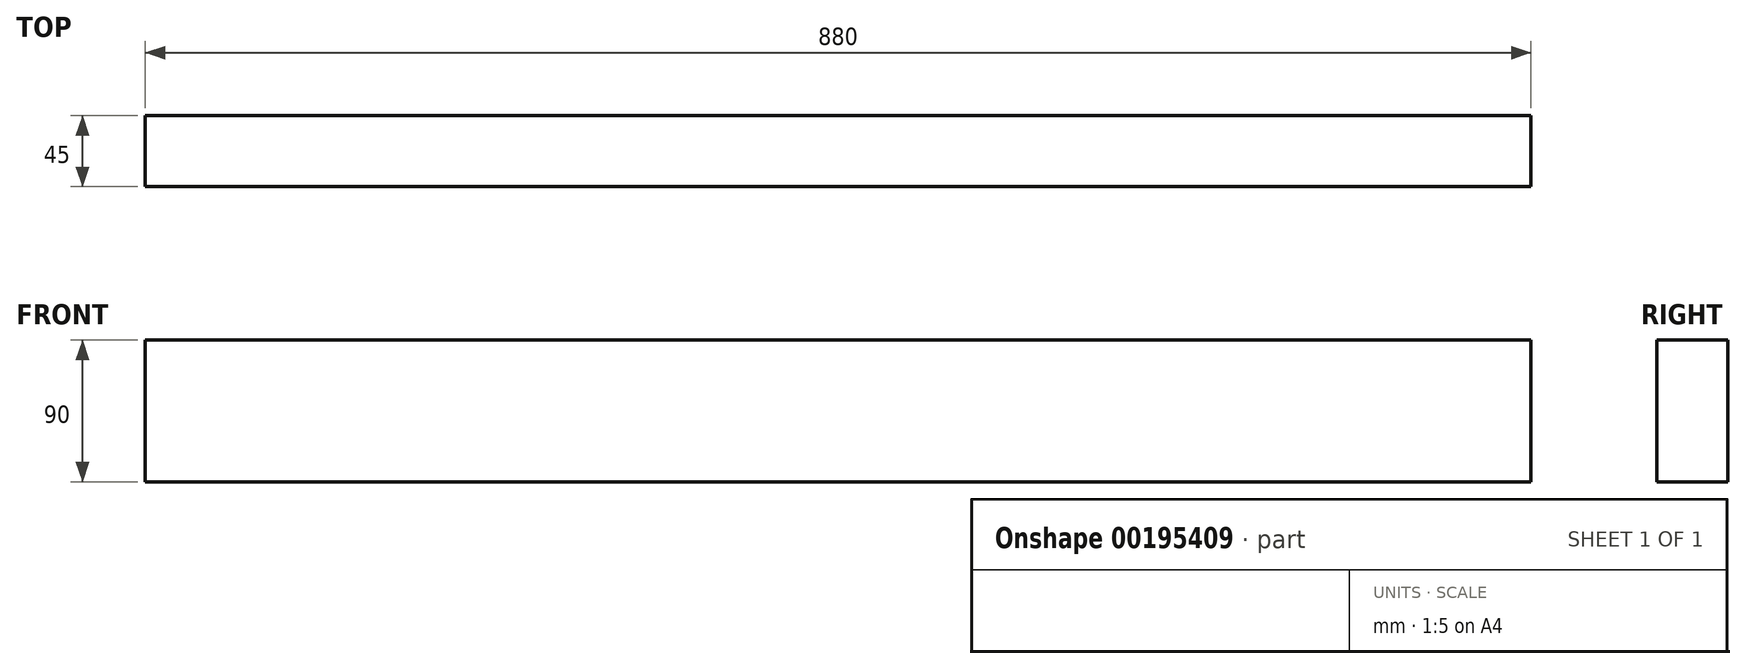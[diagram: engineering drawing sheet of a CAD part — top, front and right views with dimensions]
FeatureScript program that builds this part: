
annotation { "Feature Type Name" : "Feature", "Feature Type Description" : "" }
export const myFeature = defineFeature(function(context is Context, id is Id, definition is map)
    precondition{}
    {
        {
            var Q0;
            Q0=qCreatedBy(makeId("Front.planeOp"),FACE);
            var sketch = newSketch(context, id + "F0", { "sketchPlane" : qUnion([Q0])});
            skLineSegment(sketch, "E0.bottom", {"start": v(440, -45) * mm, "end": v(-440, -45) * mm});
            skLineSegment(sketch, "E0.top", {"start": v(440, 45) * mm, "end": v(-440, 45) * mm});
            skLineSegment(sketch, "E0.left", {"start": v(440, -45) * mm, "end": v(440, 45) * mm});
            skLineSegment(sketch, "E0.right", {"start": v(-440, -45) * mm, "end": v(-440, 45) * mm});
            skPoint(sketch, "E0.middle", {"position": v(0, 0) * mm});
            skSolve(sketch);
        }
        {
            var Q0;
            Q0=makeQuery(id+"F0.imprint","IMPRINT",FACE,{"disambiguationData":[TD([[makeQuery(id+"F0.imprint","IMPRINT",EDGE,{"derivedFrom":sQuery(id+"F0.wireOp",EDGE,"E0.bottom")}),-1.0]])]});
            extrude(context, id + "F1", {"entities" : qUnion([Q0]), "endBound" : BoundingType.SYMMETRIC, "depth" : 45 * mm});
        }
    });
